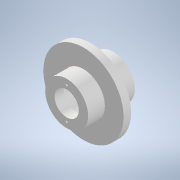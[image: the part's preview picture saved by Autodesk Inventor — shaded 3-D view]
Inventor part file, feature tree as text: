
AUTODESK INVENTOR PART (.ipt)
format: ipt  version: 2022 (Build 260153000, 153)  size: 292,352 bytes
history: native  units: mm
features: sketch x4, fillet x3, revolve x2, projected_geometry x2, hole x1, extrude x1
ambient origin geometry x8: Origin, YZ Plane, XZ Plane, XY Plane, X Axis, Y Axis, Z Axis, Center Point
bodies: Solid1 (feature_tree)
feature tree (13):
  revolve  "Revolution1"  [1 undecoded]
  hole  "Hole1"  [1 undecoded]
  extrude  "Extrusion1"  Depth=5.0mm
  revolve  "Revolution2"  [1 undecoded]
  fillet  "Fillet1"  [1 undecoded]
  fillet  "Fillet2"  Radius=17.0mm
  fillet  "Fillet3"  Radius=4.0mm
  sketch  "Sketch1"  dims[d1=11.5mm d2=9.5mm]
  sketch  "Sketch2"  dims[d3=4.0mm d4=12.0mm]
  sketch  "Sketch3"  dims[d7=25.0mm d8=5.0mm]
  projected_geometry  "Projected Loop1"
  sketch  "Sketch4"  dims[d10=10.0mm d11=6.5mm d12=90.0deg d13=17.0mm d14=1.0mm d15=6.0mm d16=4.0mm d17=2.0mm d18=90.0deg d19=8.0mm d20=20.594885mm d21=4.0mm d23=8.187861mm d24=10.0mm d25=0.0mm d27=90.0deg d28=11.5mm d29=2.0mm d30=2.0mm d31=2.0mm]
  projected_geometry  "Projected Loop2"
note: 4 required parameter values undecoded (feature->parameter linkage not recoverable at this tier; creation-order binding heuristic only, values carry confidence <= 0.55)